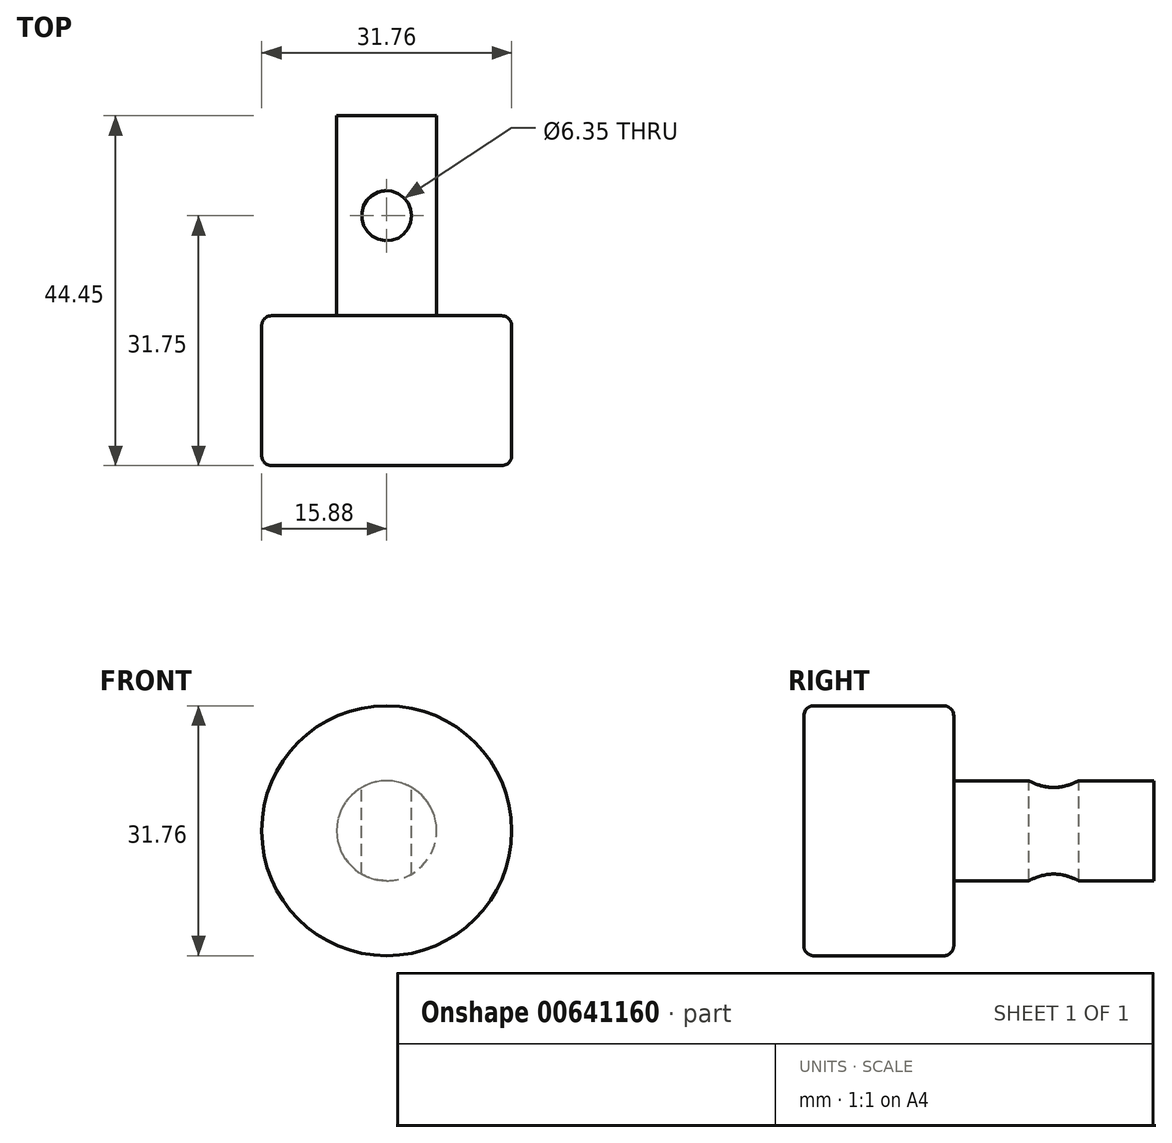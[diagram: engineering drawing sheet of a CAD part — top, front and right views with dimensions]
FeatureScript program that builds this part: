
annotation { "Feature Type Name" : "Feature", "Feature Type Description" : "" }
export const myFeature = defineFeature(function(context is Context, id is Id, definition is map)
    precondition{}
    {
        {
            var Q0;
            Q0=qCreatedBy(makeId("Front.planeOp"),FACE);
            var sketch = newSketch(context, id + "F0", { "sketchPlane" : qUnion([Q0])});
            skCircle(sketch, "E0", {"center": v(0, 0) * mm, "radius": 15.88 * mm});
            skSolve(sketch);
        }
        {
            var Q0;
            Q0 = qSketchRegion(id + "F0", true);
            extrude(context, id + "F1", {"entities" : qUnion([Q0]), "oppositeDirection" : true, "depth" : 19.05 * mm, "offsetDistance" : 25.4 * mm});
        }
        {
            var Q0;
            Q0=makeQuery(id+"F1.opExtrude","CAP_EDGE",EDGE,{"disambiguationData":[OSD([sQuery(id+"F0.wireOp",EDGE,"E0")])],"isStart":false});
            var Q1;
            Q1=makeQuery(id+"F1.opExtrude","CAP_EDGE",EDGE,{"disambiguationData":[OSD([sQuery(id+"F0.wireOp",EDGE,"E0")])],"isStart":true});
            fillet(context, id + "F2", {"entities" : qUnion([Q0, Q1]), "radius" : 1.27 * mm, "tangentPropagation" : true, "allowEdgeOverflow" : false});
        }
        {
            var Q0;
            Q0=makeQuery(id+"F1.opExtrude","CAP_FACE",FACE,{"disambiguationData":[OSD([sQuery(id+"F0.wireOp",EDGE,"E0")])],"isStart":false});
            var sketch = newSketch(context, id + "F3", { "sketchPlane" : qUnion([Q0])});
            skCircle(sketch, "E1", {"center": v(0, 0) * mm, "radius": 6.35 * mm});
            skSolve(sketch);
        }
        {
            var Q0;
            Q0 = qSketchRegion(id + "F3", true);
            extrude(context, id + "F4", {"entities" : qUnion([Q0]), "operationType" : NewBodyOperationType.ADD, "depth" : 25.4 * mm, "offsetDistance" : 25.4 * mm});
        }
        {
            var Q0;
            Q0=qCreatedBy(makeId("Top.planeOp"),FACE);
            var sketch = newSketch(context, id + "F5", { "sketchPlane" : qUnion([Q0])});
            skCircle(sketch, "E2", {"center": v(0, 31.75) * mm, "radius": 3.18 * mm});
            skSolve(sketch);
        }
        {
            var Q0;
            Q0 = qSketchRegion(id + "F5", true);
            extrude(context, id + "F6", {"entities" : qUnion([Q0]), "operationType" : NewBodyOperationType.REMOVE, "endBound" : BoundingType.SYMMETRIC, "oppositeDirection" : true, "depth" : 25.4 * mm, "offsetDistance" : 25.4 * mm});
        }
    });
